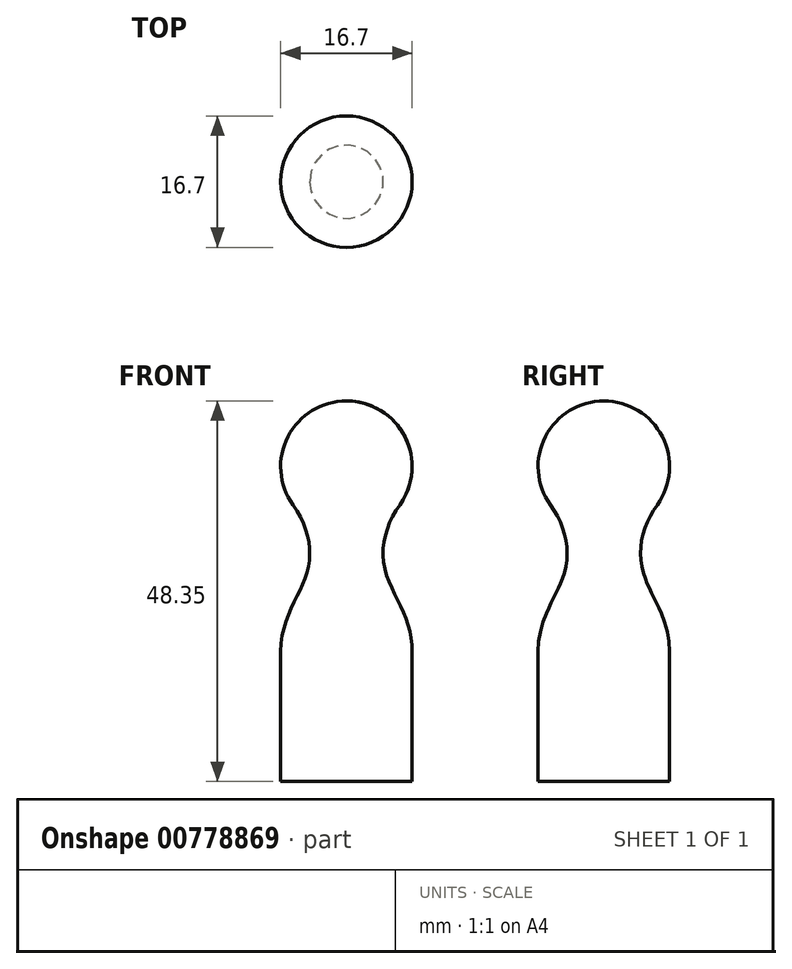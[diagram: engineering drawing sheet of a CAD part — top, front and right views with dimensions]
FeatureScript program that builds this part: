
annotation { "Feature Type Name" : "Feature", "Feature Type Description" : "" }
export const myFeature = defineFeature(function(context is Context, id is Id, definition is map)
    precondition{}
    {
        {
            var Q0;
            Q0=qCreatedBy(makeId("Front.planeOp"),FACE);
            var sketch = newSketch(context, id + "F0", { "sketchPlane" : qUnion([Q0])});
            skLineSegment(sketch, "E0", {"start": v(0, 0) * mm, "end": v(8.35, 0) * mm});
            skLineSegment(sketch, "E1", {"start": v(8.35, 0) * mm, "end": v(8.35, 16.5) * mm});
            skArc(sketch, "E2", {"start": v(6.78, 35.13) * mm, "mid": v(7.43, 43.81) * mm, "end": v(0, 48.35) * mm});
            skFitSpline(sketch, "E3", {"points": [v(8.35, 16.5) * mm, v(5, 26.59) * mm, v(6.78, 35.13) * mm], "startDerivative": vector(0, 24.77) * mm, "endDerivative": vector(12.64, 17.6) * mm});
            skLineSegment(sketch, "E4", {"start": v(0, 0) * mm, "end": v(0, 48.35) * mm});
            skSolve(sketch);
        }
        {
            var Q0;
            Q0=makeQuery(id+"F0.imprint","IMPRINT",FACE,{"disambiguationData":[TD([[makeQuery(id+"F0.imprint","IMPRINT",EDGE,{"derivedFrom":sQuery(id+"F0.wireOp",EDGE,"E0")}),1.0]])]});
            var Q1;
            Q1=sQuery(id+"F0.wireOp",EDGE,"E4");
            revolve(context, id + "F1", {"surfaceOperationType" : NewSurfaceOperationType.NEW, "entities" : qUnion([Q0]), "axis" : qUnion([Q1]), "revolveType" : RevolveType.FULL});
        }
    });
